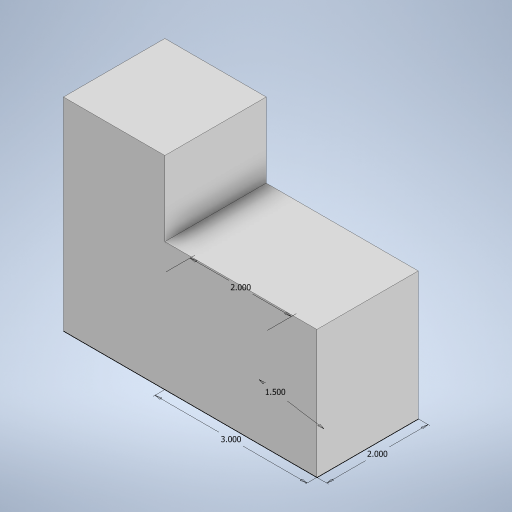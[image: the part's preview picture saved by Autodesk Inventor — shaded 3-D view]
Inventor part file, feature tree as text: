
AUTODESK INVENTOR PART (.ipt)
format: ipt  version: 2023 (Build 270158000, 158)  size: 206,848 bytes
history: native  units: in
note: dims shown in document units (in); Inventor stores cm internally (conversion verified against a paired STEP export)
features: extrude x2, sketch x1
ambient origin geometry x8: Origin, YZ Plane, XZ Plane, XY Plane, X Axis, Y Axis, Z Axis, Center Point
bodies: Solid1 (feature_tree)
feature tree (3):
  sketch  "Sketch1"  dims[d0=3.0in d1=2.0in d2=2.0in d3=1.5in d4=2.528in d5=0.0in d6=4.0in d7=0.0in]
  extrude  "Extrusion1"  Depth=2.0in
  extrude  "Extrusion2"  Depth=2.0in
